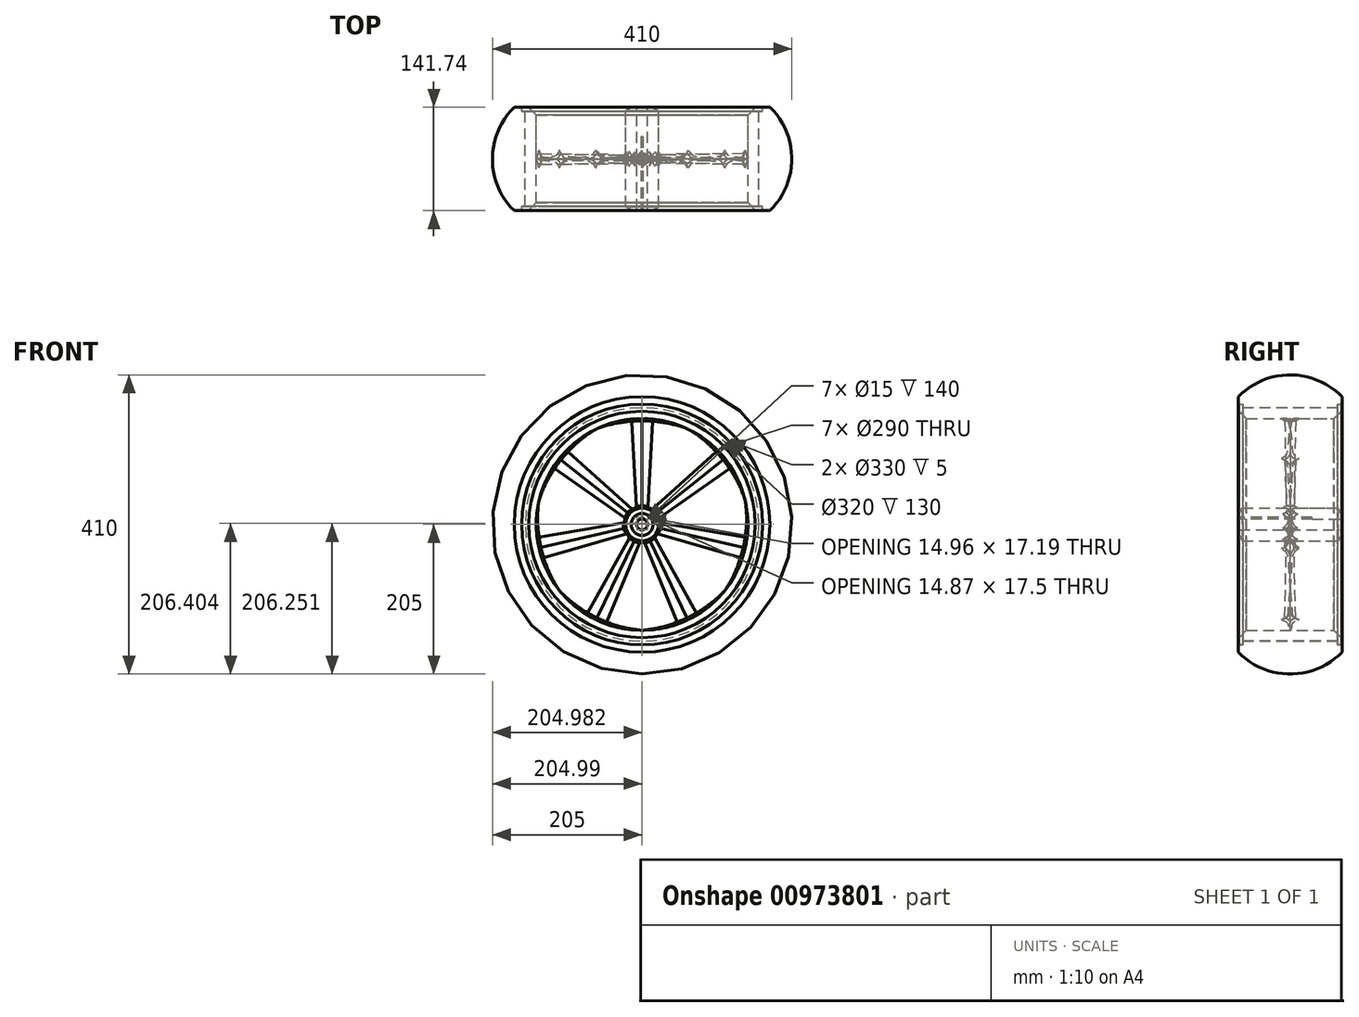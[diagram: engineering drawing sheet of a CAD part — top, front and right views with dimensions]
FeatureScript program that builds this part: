
annotation { "Feature Type Name" : "Feature", "Feature Type Description" : "" }
export const myFeature = defineFeature(function(context is Context, id is Id, definition is map)
    precondition{}
    {
        {
            var Q0;
            Q0=qCreatedBy(makeId("Right.planeOp"),FACE);
            var sketch = newSketch(context, id + "F0", { "sketchPlane" : qUnion([Q0])});
            skLineSegment(sketch, "E0", {"start": v(70, 0) * mm, "end": v(-70, 0) * mm, "construction": true});
            skLineSegment(sketch, "E1", {"start": v(-70, 0) * mm, "end": v(-70, 7.5) * mm, "construction": true});
            skLineSegment(sketch, "E2", {"start": v(-70, 7.5) * mm, "end": v(70, 7.5) * mm});
            skLineSegment(sketch, "E3", {"start": v(70, 7.5) * mm, "end": v(70, 0) * mm, "construction": true});
            skLineSegment(sketch, "E4", {"start": v(-70, 7.5) * mm, "end": v(-70, 15) * mm});
            skLineSegment(sketch, "E5", {"start": v(-70, 15) * mm, "end": v(-65.67, 22.5) * mm});
            skLineSegment(sketch, "E6", {"start": v(-65.67, 22.5) * mm, "end": v(65.67, 22.5) * mm});
            skLineSegment(sketch, "E7", {"start": v(70, 15) * mm, "end": v(70, 7.5) * mm});
            skPoint(sketch, "E8.visualSharp", {"position": v(65.67, 22.5) * mm});
            skPoint(sketch, "E9.visualSharp", {"position": v(-65.67, 22.5) * mm});
            skLineSegment(sketch, "E10", {"start": v(0, 0) * mm, "end": v(0, 160) * mm, "construction": true});
            skLineSegment(sketch, "E11", {"start": v(0, 145) * mm, "end": v(60, 145) * mm});
            skLineSegment(sketch, "E12", {"start": v(0, 145) * mm, "end": v(-60, 145) * mm});
            skLineSegment(sketch, "E13", {"start": v(70, 160) * mm, "end": v(70, 155) * mm});
            skLineSegment(sketch, "E14", {"start": v(70, 155) * mm, "end": v(60, 145) * mm});
            skLineSegment(sketch, "E15", {"start": v(-70, 203.2) * mm, "end": v(-70, 155) * mm});
            skLineSegment(sketch, "E16", {"start": v(-60, 145) * mm, "end": v(-70, 155) * mm});
            skPoint(sketch, "E17.visualSharp", {"position": v(60, 145) * mm});
            skLineSegment(sketch, "E18", {"start": v(70, 160) * mm, "end": v(70, 165) * mm});
            skLineSegment(sketch, "E19", {"start": v(70, 165) * mm, "end": v(65, 165) * mm});
            skLineSegment(sketch, "E20", {"start": v(65, 165) * mm, "end": v(65, 160) * mm});
            skLineSegment(sketch, "E21", {"start": v(65, 160) * mm, "end": v(0, 160) * mm});
            skLineSegment(sketch, "E22", {"start": v(0, 160) * mm, "end": v(-65, 160) * mm});
            skLineSegment(sketch, "E23", {"start": v(-65, 160) * mm, "end": v(-65, 165) * mm});
            skLineSegment(sketch, "E24", {"start": v(-65, 165) * mm, "end": v(-70, 165) * mm});
            skLineSegment(sketch, "E25", {"start": v(-70, 203.2) * mm, "end": v(-70, 165) * mm});
            skLineSegment(sketch, "E26", {"start": v(70, 15) * mm, "end": v(65.67, 22.5) * mm});
            skSolve(sketch);
        }
        {
            var Q0;
            Q0=makeQuery(id+"F0.imprint","IMPRINT",FACE,{"disambiguationData":[TD([[makeQuery(id+"F0.imprint","IMPRINT",EDGE,{"derivedFrom":sQuery(id+"F0.wireOp",EDGE,"E11")}),1.0]])]});
            var Q1;
            Q1=makeQuery(id+"F0.imprint","IMPRINT",FACE,{"disambiguationData":[TD([[makeQuery(id+"F0.imprint","IMPRINT",EDGE,{"derivedFrom":sQuery(id+"F0.wireOp",EDGE,"E2")}),1.0]])]});
            var Q2;
            Q2=sQuery(id+"F0.wireOp",EDGE,"E0");
            revolve(context, id + "F1", {"surfaceOperationType" : NewSurfaceOperationType.NEW, "entities" : qUnion([Q0, Q1]), "axis" : qUnion([Q2]), "revolveType" : RevolveType.FULL});
        }
        {
            var Q0;
            Q0=qCreatedBy(makeId("Top.planeOp"),FACE);
            cPlane(context, id + "F2", {"entities" : qUnion([Q0]), "cplaneType" : CPlaneType.OFFSET, "offset" : 150 * mm, "width" : 150 * mm, "height" : 150 * mm});
        }
        {
            var Q0;
            Q0=qCreatedBy(id+"F2.planeOp",FACE);
            var sketch = newSketch(context, id + "F3", { "sketchPlane" : qUnion([Q0])});
            skLineSegment(sketch, "E27", {"start": v(0, 0) * mm, "end": v(15, 0) * mm, "construction": true});
            skLineSegment(sketch, "E28", {"start": v(0, 0) * mm, "end": v(0, 7.5) * mm, "construction": true});
            skArc(sketch, "E29", {"start": v(0, 7.5) * mm, "mid": v(6.68, 2.1) * mm, "end": v(15, 0) * mm});
            skArc(sketch, "E30.MirrorCS", {"start": v(0, -7.5) * mm, "mid": v(6.68, -2.1) * mm, "end": v(15, 0) * mm});
            skArc(sketch, "E31.MirrorCS", {"start": v(0, 7.5) * mm, "mid": v(-6.68, 2.1) * mm, "end": v(-15, 0) * mm});
            skArc(sketch, "E32.MirrorCS", {"start": v(0, -7.5) * mm, "mid": v(-6.68, -2.1) * mm, "end": v(-15, 0) * mm});
            skSolve(sketch);
        }
        {
            var Q0;
            Q0=qCreatedBy(makeId("Top.planeOp"),FACE);
            cPlane(context, id + "F4", {"entities" : qUnion([Q0]), "cplaneType" : CPlaneType.OFFSET, "offset" : 20 * mm, "width" : 150 * mm, "height" : 150 * mm});
        }
        {
            var Q0;
            Q0=qCreatedBy(id+"F4.planeOp",FACE);
            var sketch = newSketch(context, id + "F5", { "sketchPlane" : qUnion([Q0])});
            skArc(sketch, "E33", {"start": v(0, 5) * mm, "mid": v(3.46, 2.07) * mm, "end": v(7.5, 0) * mm});
            skArc(sketch, "E34.MirrorCS", {"start": v(0, -5) * mm, "mid": v(3.46, -2.07) * mm, "end": v(7.5, 0) * mm});
            skArc(sketch, "E35.MirrorCS", {"start": v(0, 5) * mm, "mid": v(-3.46, 2.07) * mm, "end": v(-7.5, 0) * mm});
            skArc(sketch, "E36.MirrorCS", {"start": v(0, -5) * mm, "mid": v(-3.46, -2.07) * mm, "end": v(-7.5, 0) * mm});
            skLineSegment(sketch, "E37", {"start": v(0, 0) * mm, "end": v(0, -5) * mm, "construction": true});
            skLineSegment(sketch, "E38", {"start": v(0, 5) * mm, "end": v(0, 0) * mm, "construction": true});
            skLineSegment(sketch, "E39", {"start": v(0, 0) * mm, "end": v(7.5, 0) * mm, "construction": true});
            skLineSegment(sketch, "E40", {"start": v(0, 0) * mm, "end": v(-7.5, 0) * mm, "construction": true});
            skLineSegment(sketch, "E41", {"start": v(0, 0) * mm, "end": v(-14.56, 0) * mm, "construction": true});
            skLineSegment(sketch, "E42", {"start": v(-14.56, 0) * mm, "end": v(-14.56, -18.71) * mm, "construction": true});
            skSolve(sketch);
        }
        {
            var Q1;
            Q1=makeQuery(id+"F3.imprint","IMPRINT",FACE,{"disambiguationData":[TD([[makeQuery(id+"F3.imprint","IMPRINT",EDGE,{"derivedFrom":sQuery(id+"F3.wireOp",EDGE,"E29")}),-1.0]])]});
            var Q2;
            Q2=makeQuery(id+"F5.imprint","IMPRINT",FACE,{"disambiguationData":[TD([[makeQuery(id+"F5.imprint","IMPRINT",EDGE,{"derivedFrom":sQuery(id+"F5.wireOp",EDGE,"E33")}),-1.0]])]});
            loft(context, id + "F6", {"operationType" : NewBodyOperationType.ADD, "sheetProfilesArray" : [{ "sheetProfileEntities" : qUnion([Q1]) }, { "sheetProfileEntities" : qUnion([Q2]) }]});
        }
        {
            var Q0;
            Q0=makeQuery(id+"F6.boolean.opBoolean","INTERSECT",EDGE,{"derivedFrom":[makeQuery(id+"F1.opRevolve","SWEPT_FACE",FACE,{"disambiguationData":[OSD([sQuery(id+"F0.wireOp",EDGE,"E6")])]}),makeQuery(id+"F6.opLoft","SWEPT_FACE",FACE,{"disambiguationData":[OSD([sQuery(id+"F3.wireOp",EDGE,"E29"),sQuery(id+"F3.wireOp",EDGE,"E30.MirrorCS"),sQuery(id+"F3.wireOp",EDGE,"E32.MirrorCS"),sQuery(id+"F5.wireOp",EDGE,"E33"),sQuery(id+"F5.wireOp",EDGE,"E34.MirrorCS"),sQuery(id+"F5.wireOp",EDGE,"E36.MirrorCS")])]})]});
            var Q1;
            Q1=makeQuery(id+"F6.boolean.opBoolean","INTERSECT",EDGE,{"derivedFrom":[makeQuery(id+"F1.opRevolve","SWEPT_FACE",FACE,{"disambiguationData":[OSD([sQuery(id+"F0.wireOp",EDGE,"E6")])]}),makeQuery(id+"F6.opLoft","SWEPT_FACE",FACE,{"disambiguationData":[OSD([sQuery(id+"F3.wireOp",EDGE,"E30.MirrorCS"),sQuery(id+"F3.wireOp",EDGE,"E31.MirrorCS"),sQuery(id+"F3.wireOp",EDGE,"E32.MirrorCS"),sQuery(id+"F5.wireOp",EDGE,"E34.MirrorCS"),sQuery(id+"F5.wireOp",EDGE,"E35.MirrorCS"),sQuery(id+"F5.wireOp",EDGE,"E36.MirrorCS")])]})]});
            var Q2;
            Q2=makeQuery(id+"F6.boolean.opBoolean","INTERSECT",EDGE,{"derivedFrom":[makeQuery(id+"F1.opRevolve","SWEPT_FACE",FACE,{"disambiguationData":[OSD([sQuery(id+"F0.wireOp",EDGE,"E6")])]}),makeQuery(id+"F6.opLoft","SWEPT_FACE",FACE,{"disambiguationData":[OSD([sQuery(id+"F3.wireOp",EDGE,"E29"),sQuery(id+"F3.wireOp",EDGE,"E30.MirrorCS"),sQuery(id+"F3.wireOp",EDGE,"E31.MirrorCS"),sQuery(id+"F5.wireOp",EDGE,"E33"),sQuery(id+"F5.wireOp",EDGE,"E34.MirrorCS"),sQuery(id+"F5.wireOp",EDGE,"E35.MirrorCS")])]})]});
            var Q3;
            Q3=makeQuery(id+"F6.boolean.opBoolean","INTERSECT",EDGE,{"derivedFrom":[makeQuery(id+"F1.opRevolve","SWEPT_FACE",FACE,{"disambiguationData":[OSD([sQuery(id+"F0.wireOp",EDGE,"E6")])]}),makeQuery(id+"F6.opLoft","SWEPT_FACE",FACE,{"disambiguationData":[OSD([sQuery(id+"F3.wireOp",EDGE,"E29"),sQuery(id+"F3.wireOp",EDGE,"E31.MirrorCS"),sQuery(id+"F3.wireOp",EDGE,"E32.MirrorCS"),sQuery(id+"F5.wireOp",EDGE,"E33"),sQuery(id+"F5.wireOp",EDGE,"E35.MirrorCS"),sQuery(id+"F5.wireOp",EDGE,"E36.MirrorCS")])]})]});
            var Q4;
            Q4=makeQuery(id+"F6.boolean.opBoolean","INTERSECT",EDGE,{"derivedFrom":[makeQuery(id+"F1.opRevolve","SWEPT_FACE",FACE,{"disambiguationData":[OSD([sQuery(id+"F0.wireOp",EDGE,"E11"),sQuery(id+"F0.wireOp",EDGE,"E12")])]}),makeQuery(id+"F6.opLoft","SWEPT_FACE",FACE,{"disambiguationData":[OSD([sQuery(id+"F3.wireOp",EDGE,"E30.MirrorCS"),sQuery(id+"F3.wireOp",EDGE,"E31.MirrorCS"),sQuery(id+"F3.wireOp",EDGE,"E32.MirrorCS"),sQuery(id+"F5.wireOp",EDGE,"E34.MirrorCS"),sQuery(id+"F5.wireOp",EDGE,"E35.MirrorCS"),sQuery(id+"F5.wireOp",EDGE,"E36.MirrorCS")])]})]});
            var Q5;
            Q5=makeQuery(id+"F6.boolean.opBoolean","INTERSECT",EDGE,{"derivedFrom":[makeQuery(id+"F1.opRevolve","SWEPT_FACE",FACE,{"disambiguationData":[OSD([sQuery(id+"F0.wireOp",EDGE,"E11"),sQuery(id+"F0.wireOp",EDGE,"E12")])]}),makeQuery(id+"F6.opLoft","SWEPT_FACE",FACE,{"disambiguationData":[OSD([sQuery(id+"F3.wireOp",EDGE,"E29"),sQuery(id+"F3.wireOp",EDGE,"E30.MirrorCS"),sQuery(id+"F3.wireOp",EDGE,"E32.MirrorCS"),sQuery(id+"F5.wireOp",EDGE,"E33"),sQuery(id+"F5.wireOp",EDGE,"E34.MirrorCS"),sQuery(id+"F5.wireOp",EDGE,"E36.MirrorCS")])]})]});
            var Q6;
            Q6=makeQuery(id+"F6.boolean.opBoolean","INTERSECT",EDGE,{"derivedFrom":[makeQuery(id+"F1.opRevolve","SWEPT_FACE",FACE,{"disambiguationData":[OSD([sQuery(id+"F0.wireOp",EDGE,"E11"),sQuery(id+"F0.wireOp",EDGE,"E12")])]}),makeQuery(id+"F6.opLoft","SWEPT_FACE",FACE,{"disambiguationData":[OSD([sQuery(id+"F3.wireOp",EDGE,"E29"),sQuery(id+"F3.wireOp",EDGE,"E31.MirrorCS"),sQuery(id+"F3.wireOp",EDGE,"E32.MirrorCS"),sQuery(id+"F5.wireOp",EDGE,"E33"),sQuery(id+"F5.wireOp",EDGE,"E35.MirrorCS"),sQuery(id+"F5.wireOp",EDGE,"E36.MirrorCS")])]})]});
            var Q7;
            Q7=makeQuery(id+"F6.boolean.opBoolean","INTERSECT",EDGE,{"derivedFrom":[makeQuery(id+"F1.opRevolve","SWEPT_FACE",FACE,{"disambiguationData":[OSD([sQuery(id+"F0.wireOp",EDGE,"E11"),sQuery(id+"F0.wireOp",EDGE,"E12")])]}),makeQuery(id+"F6.opLoft","SWEPT_FACE",FACE,{"disambiguationData":[OSD([sQuery(id+"F3.wireOp",EDGE,"E29"),sQuery(id+"F3.wireOp",EDGE,"E30.MirrorCS"),sQuery(id+"F3.wireOp",EDGE,"E31.MirrorCS"),sQuery(id+"F5.wireOp",EDGE,"E33"),sQuery(id+"F5.wireOp",EDGE,"E34.MirrorCS"),sQuery(id+"F5.wireOp",EDGE,"E35.MirrorCS")])]})]});
            chamfer(context, id + "F7", {"entities" : qUnion([Q0, Q1, Q2, Q3, Q4, Q5, Q6, Q7]), "width" : 3 * mm, "tangentPropagation" : true});
        }
        {
            var Q0;
            Q0=makeQuery(id+"F1.opRevolve","SWEPT_BODY",BODY,{"disambiguationData":[OSD([sQuery(id+"F0.wireOp",EDGE,"E2"),sQuery(id+"F0.wireOp",EDGE,"E4"),sQuery(id+"F0.wireOp",EDGE,"E5"),sQuery(id+"F0.wireOp",EDGE,"E6"),sQuery(id+"F0.wireOp",EDGE,"fgmkqya3-Bmk3-VCuH-b24Y-oyjxGJAGjQBz"),sQuery(id+"F0.wireOp",EDGE,"E7"),sQuery(id+"F0.wireOp",EDGE,"E8.filletArc"),sQuery(id+"F0.wireOp",EDGE,"E9.filletArc")])]});
            var Q1;
            Q1=makeQuery(id+"F1.opRevolve","SWEPT_EDGE",EDGE,{"disambiguationData":[OSD([sQuery(id+"F0.wireOp",EDGE,"E2"),sQuery(id+"F0.wireOp",EDGE,"E4")])]});
            circularPattern(context, id + "F8", {"entities" : qUnion([Q0]), "axis" : qUnion([Q1]), "angle" : 360 * degree, "instanceCount" : 7, "equalSpace" : true, "computeTransformsWithoutBuiltin" : true});
        }
        {
            var Q0;
            Q0=qCreatedBy(makeId("Right.planeOp"),FACE);
            var sketch = newSketch(context, id + "F9", { "sketchPlane" : qUnion([Q0])});
            skLineSegment(sketch, "E43", {"start": v(44.4, -102.1) * mm, "end": v(44.4, -102.1) * mm});
            skPoint(sketch, "E44.visualSharp", {"position": v(44.4, -102.1) * mm});
            skLineSegment(sketch, "E45", {"start": v(0, 0) * mm, "end": v(0, 160) * mm, "construction": true});
            skLineSegment(sketch, "E46", {"start": v(70, 165) * mm, "end": v(65, 165) * mm});
            skLineSegment(sketch, "E47", {"start": v(65, 165) * mm, "end": v(65, 160) * mm});
            skLineSegment(sketch, "E48", {"start": v(65, 160) * mm, "end": v(0, 160) * mm});
            skLineSegment(sketch, "E49", {"start": v(0, 160) * mm, "end": v(-65, 160) * mm});
            skLineSegment(sketch, "E50", {"start": v(-65, 160) * mm, "end": v(-65, 165) * mm});
            skLineSegment(sketch, "E51", {"start": v(-65, 165) * mm, "end": v(-70, 165) * mm});
            skLineSegment(sketch, "E52", {"start": v(-70, 165) * mm, "end": v(-70.87, 175) * mm});
            skLineSegment(sketch, "E53", {"start": v(70, 165) * mm, "end": v(70.87, 175) * mm});
            skArc(sketch, "E54", {"start": v(70.87, 175) * mm, "mid": v(0, 205) * mm, "end": v(-70.87, 175) * mm});
            skLineSegment(sketch, "E55", {"start": v(-69.67, 0) * mm, "end": v(91.66, 0) * mm, "construction": true});
            skSolve(sketch);
        }
        {
            var Q0;
            Q0=makeQuery(id+"F9.imprint","IMPRINT",FACE,{"disambiguationData":[TD([[makeQuery(id+"F9.imprint","IMPRINT",EDGE,{"derivedFrom":sQuery(id+"F9.wireOp",EDGE,"E46")}),-1.0]])]});
            var Q1;
            Q1=sQuery(id+"F9.wireOp",EDGE,"E55");
            revolve(context, id + "F10", {"surfaceOperationType" : NewSurfaceOperationType.NEW, "entities" : qUnion([Q0]), "axis" : qUnion([Q1]), "revolveType" : RevolveType.FULL});
        }
        {
            var Q0;
            Q0=makeQuery(id+"F1.opRevolve","SWEPT_FACE",FACE,{"disambiguationData":[OSD([sQuery(id+"F0.wireOp",EDGE,"E4")])]});
            var sketch = newSketch(context, id + "F11", { "sketchPlane" : qUnion([Q0])});
            skCircle(sketch, "E56", {"center": v(0, 0) * mm, "radius": 7.5 * mm});
            skArc(sketch, "E57", {"start": v(1.25, 9.92) * mm, "mid": v(0, 10) * mm, "end": v(-1.25, 9.92) * mm});
            skLineSegment(sketch, "E58", {"start": v(0, 0) * mm, "end": v(0, 10) * mm, "construction": true});
            skLineSegment(sketch, "E59", {"start": v(-1.25, 7.4) * mm, "end": v(-1.25, 9.92) * mm});
            skLineSegment(sketch, "E60", {"start": v(1.25, 7.4) * mm, "end": v(1.25, 9.92) * mm});
            skPoint(sketch, "E61", {"position": v(-1.25, 7.4) * mm});
            skPoint(sketch, "E62", {"position": v(1.25, 7.4) * mm});
            skPoint(sketch, "E63", {"position": v(-1.25, 9.92) * mm});
            skPoint(sketch, "E64", {"position": v(1.25, 9.92) * mm});
            skPoint(sketch, "E65.orphan", {"position": v(-1.25, 0) * mm});
            skPoint(sketch, "E66.orphan", {"position": v(1.25, 0) * mm});
            skSolve(sketch);
        }
        {
            var Q0;
            Q0=qSketchRegion(id+"F11",true);
            extrude(context, id + "F12", {"entities" : qUnion([Q0]), "operationType" : NewBodyOperationType.REMOVE, "oppositeDirection" : true, "depth" : 100 * mm, "offsetDistance" : 25 * mm});
        }
    });
